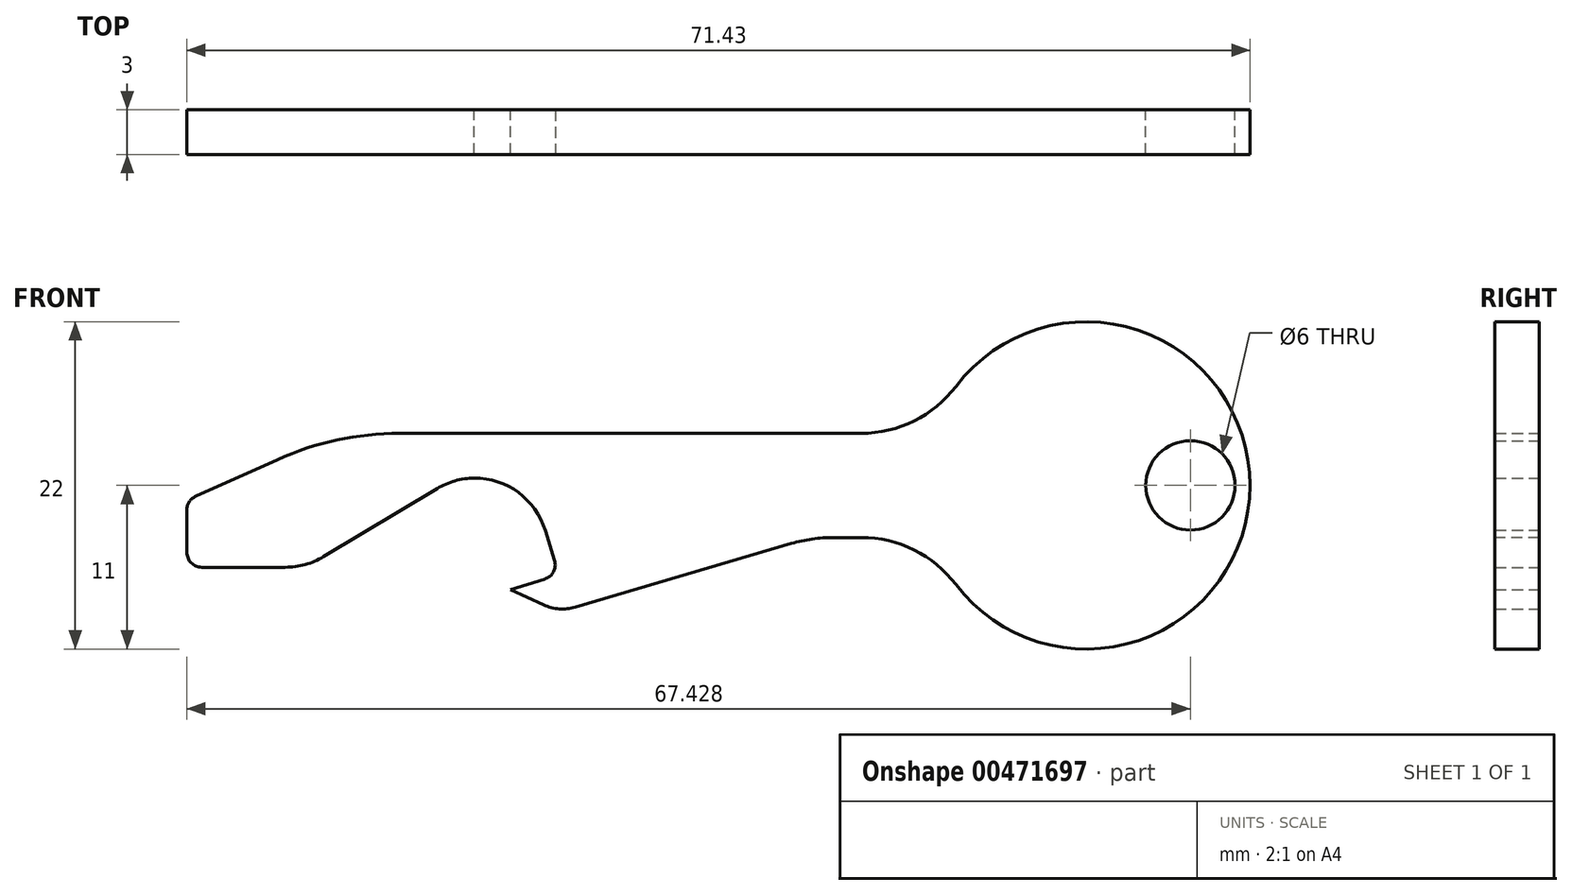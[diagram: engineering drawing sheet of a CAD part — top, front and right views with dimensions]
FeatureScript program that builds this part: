
annotation { "Feature Type Name" : "Feature", "Feature Type Description" : "" }
export const myFeature = defineFeature(function(context is Context, id is Id, definition is map)
    precondition{}
    {
        {
            var Q0;
            Q0=qCreatedBy(makeId("Front.planeOp"),FACE);
            var sketch = newSketch(context, id + "F0", { "sketchPlane" : qUnion([Q0])});
            skLineSegment(sketch, "E0.bottom", {"start": v(0, 0) * mm, "end": v(40, 0) * mm});
            skLineSegment(sketch, "E0.top", {"start": v(0, 7) * mm, "end": v(40, 7) * mm});
            skLineSegment(sketch, "E0.left", {"start": v(0, 0) * mm, "end": v(0, 7) * mm});
            skLineSegment(sketch, "E0.right", {"start": v(40, 0) * mm, "end": v(40, 7) * mm});
            skArc(sketch, "E1", {"start": v(40, 0) * mm, "mid": v(61.43, 3.5) * mm, "end": v(40, 7) * mm});
            skLineSegment(sketch, "E2", {"start": v(0, 7) * mm, "end": v(-10, 2.5) * mm});
            skLineSegment(sketch, "E3", {"start": v(-10, 2.5) * mm, "end": v(-10, -2) * mm});
            skLineSegment(sketch, "E4", {"start": v(-10, -2) * mm, "end": v(-2, -2) * mm});
            skLineSegment(sketch, "E5", {"start": v(-2, -2) * mm, "end": v(8, 4) * mm});
            skLineSegment(sketch, "E6", {"start": v(8, 4) * mm, "end": v(13, 4) * mm});
            skLineSegment(sketch, "E7", {"start": v(13, 4) * mm, "end": v(15, -2.5) * mm});
            skLineSegment(sketch, "E8", {"start": v(15, -2.5) * mm, "end": v(11.75, -3.5) * mm});
            skLineSegment(sketch, "E9", {"start": v(11.75, -3.5) * mm, "end": v(15, -5) * mm});
            skLineSegment(sketch, "E10", {"start": v(15, -5) * mm, "end": v(32, 0) * mm});
            skCircle(sketch, "E11", {"center": v(57.43, 3.5) * mm, "radius": 3 * mm});
            skSolve(sketch);
        }
        {
            var Q0;
            {var subQ0=sQuery(id+"F0.wireOp",EDGE,"E0.left");Q0=makeQuery(id+"F0.imprint","IMPRINT",FACE,{"disambiguationData":[TD([[makeQuery(id+"F0.imprint","IMPRINT",EDGE,{"derivedFrom":subQ0}),1.0]])]});}
            var Q1;
            {var subQ9=sQuery(id+"F0.wireOp",EDGE,"E0.left");Q1=makeQuery(id+"F0.imprint","IMPRINT",FACE,{"disambiguationData":[TD([[makeQuery(id+"F0.imprint","IMPRINT",EDGE,{"derivedFrom":subQ9}),-1.0]])]});}
            var Q2;
            {var subQ4=sQuery(id+"F0.wireOp",EDGE,"E8");Q2=makeQuery(id+"F0.imprint","IMPRINT",FACE,{"disambiguationData":[TD([[makeQuery(id+"F0.imprint","IMPRINT",EDGE,{"derivedFrom":subQ4}),1.0]])]});}
            var Q3;
            {var subQ3=sQuery(id+"F0.wireOp",EDGE,"7VBHRefb-ZezH-LXmD-XGCx-hcoTWlabLQlG");Q3=makeQuery(id+"F0.imprint","IMPRINT",FACE,{"disambiguationData":[TD([[makeQuery(id+"F0.imprint","IMPRINT",EDGE,{"derivedFrom":subQ3}),-1.0]])]});}
            var Q4;
            {var subQ3=sQuery(id+"F0.wireOp",EDGE,"lKG2LDTI-TQmS-NmJ1-liUh-qlYl0mUGQLIu");Q4=makeQuery(id+"F0.imprint","IMPRINT",FACE,{"disambiguationData":[TD([[makeQuery(id+"F0.imprint","IMPRINT",EDGE,{"derivedFrom":subQ3}),-1.0]])]});}
            var Q5;
            {var subQ0=sQuery(id+"F0.wireOp",EDGE,"E0.right");Q5=makeQuery(id+"F0.imprint","IMPRINT",FACE,{"disambiguationData":[TD([[makeQuery(id+"F0.imprint","IMPRINT",EDGE,{"derivedFrom":subQ0}),1.0]])]});}
            var Q6;
            {var subQ0=sQuery(id+"F0.wireOp",EDGE,"E0.right");Q6=makeQuery(id+"F0.imprint","IMPRINT",FACE,{"disambiguationData":[TD([[makeQuery(id+"F0.imprint","IMPRINT",EDGE,{"derivedFrom":subQ0}),-1.0]])]});}
            extrude(context, id + "F1", {"entities" : qUnion([Q0, Q1, Q2, Q3, Q4, Q5, Q6]), "depth" : 3 * mm});
        }
        {
            var Q0;
            Q0=makeQuery(id+"F1.opExtrude","SWEPT_EDGE",EDGE,{"disambiguationData":[OSD([sQuery(id+"F0.wireOp",EDGE,"E0.bottom"),sQuery(id+"F0.wireOp",EDGE,"E10")])]});
            fillet(context, id + "F2", {"entities" : qUnion([Q0]), "radius" : 10 * mm, "tangentPropagation" : true, "allowEdgeOverflow" : false});
        }
        {
            var Q0;
            Q0=makeQuery(id+"F1.opExtrude","SWEPT_EDGE",EDGE,{"disambiguationData":[OSD([sQuery(id+"F0.wireOp",EDGE,"E6"),sQuery(id+"F0.wireOp",EDGE,"E7")])]});
            var Q1;
            Q1=makeQuery(id+"F1.opExtrude","SWEPT_EDGE",EDGE,{"disambiguationData":[OSD([sQuery(id+"F0.wireOp",EDGE,"E4"),sQuery(id+"F0.wireOp",EDGE,"E5")])]});
            fillet(context, id + "F3", {"entities" : qUnion([Q0, Q1]), "radius" : 5 * mm, "tangentPropagation" : true, "allowEdgeOverflow" : false});
        }
        {
            var Q0;
            Q0=makeQuery(id+"F1.opExtrude","SWEPT_EDGE",EDGE,{"disambiguationData":[OSD([sQuery(id+"F0.wireOp",EDGE,"E7"),sQuery(id+"F0.wireOp",EDGE,"E8")])]});
            fillet(context, id + "F4", {"entities" : qUnion([Q0]), "radius" : 1 * mm, "tangentPropagation" : true, "allowEdgeOverflow" : false});
        }
        {
            var Q0;
            Q0=makeQuery(id+"F1.opExtrude","SWEPT_EDGE",EDGE,{"disambiguationData":[OSD([sQuery(id+"F0.wireOp",EDGE,"E5"),sQuery(id+"F0.wireOp",EDGE,"E6")])]});
            fillet(context, id + "F5", {"entities" : qUnion([Q0]), "radius" : 5 * mm, "tangentPropagation" : true, "allowEdgeOverflow" : false});
        }
        {
            var Q0;
            Q0=makeQuery(id+"F1.opExtrude","SWEPT_EDGE",EDGE,{"disambiguationData":[OSD([sQuery(id+"F0.wireOp",EDGE,"E0.top"),sQuery(id+"F0.wireOp",EDGE,"E0.left"),sQuery(id+"F0.wireOp",EDGE,"E2")])]});
            fillet(context, id + "F6", {"entities" : qUnion([Q0]), "radius" : 20 * mm, "tangentPropagation" : true, "allowEdgeOverflow" : false});
        }
        {
            var Q0;
            Q0=makeQuery(id+"F1.opExtrude","SWEPT_EDGE",EDGE,{"disambiguationData":[OSD([sQuery(id+"F0.wireOp",EDGE,"E2"),sQuery(id+"F0.wireOp",EDGE,"E3")])]});
            var Q1;
            Q1=makeQuery(id+"F1.opExtrude","SWEPT_EDGE",EDGE,{"disambiguationData":[OSD([sQuery(id+"F0.wireOp",EDGE,"E3"),sQuery(id+"F0.wireOp",EDGE,"E4")])]});
            fillet(context, id + "F7", {"entities" : qUnion([Q0, Q1]), "radius" : 1 * mm, "tangentPropagation" : true, "allowEdgeOverflow" : false});
        }
        {
            var Q0;
            Q0=makeQuery(id+"F1.opExtrude","SWEPT_EDGE",EDGE,{"disambiguationData":[OSD([sQuery(id+"F0.wireOp",EDGE,"E9"),sQuery(id+"F0.wireOp",EDGE,"E10")])]});
            fillet(context, id + "F8", {"entities" : qUnion([Q0]), "radius" : 3 * mm, "tangentPropagation" : true, "allowEdgeOverflow" : false});
        }
        {
            var Q0;
            Q0=makeQuery(id+"F1.opExtrude","SWEPT_EDGE",EDGE,{"disambiguationData":[OSD([sQuery(id+"F0.wireOp",EDGE,"E0.top"),sQuery(id+"F0.wireOp",EDGE,"E0.right"),sQuery(id+"F0.wireOp",EDGE,"E1")])]});
            var Q1;
            Q1=makeQuery(id+"F1.opExtrude","SWEPT_EDGE",EDGE,{"disambiguationData":[OSD([sQuery(id+"F0.wireOp",EDGE,"E0.bottom"),sQuery(id+"F0.wireOp",EDGE,"E0.right"),sQuery(id+"F0.wireOp",EDGE,"E1")])]});
            fillet(context, id + "F9", {"entities" : qUnion([Q0, Q1]), "radius" : 8 * mm, "tangentPropagation" : true, "allowEdgeOverflow" : false});
        }
    });
